# Revit family: Haworth_BeHold_StackOnBookcase
name_source: partatom
category: Furniture Systems
revit_build: Autodesk Revit 2018 (Build: 20170223_1515(x64)
units: mm (PartAtom-declared; Revit-internal decimal feet)

## family parameters
Always vertical = Yes
Cut with Voids When Loaded = No
OmniClass Number = 23.40.70.14.64.21
OmniClass Title = Systems Furniture
Part Type = Normal
Room Calculation Point = No
Round Connector Dimension = Use Diameter
Shared = No
Work Plane-Based = No

## types (6) — shared parameters
Actual Depth = 16 "
Actual Shelf 1 = Yes
Actual Width = 36 "
Assembly Code = E2020200
Base Height = 0.75 "
Cabinet Finish = Haworth _ Laminate _ Beige H-34
Custom Size = No
Description = Haworth - Be_Hold - Upper Storage - Stack on Bookcase
Inset Style Width = 15.81 "
Manufacturer = Haworth
Max. Height = 59 "
Max. Width = 36 "
Min. Height = 20 "
Min. Width = 18 "
Model = Haworth Be_Hold
Mounting Height = 22 "
Panel Thickness = 0.75 "
Revision Number = 1
Shelf Depth = 15.25 "
Shelf Height 3 = 15.25 "
Shelf Width = 34.5 "
Size = Verify Final Dim. w/ Haworth
Standard Depths = 16
Standard Height = 20-59 in.
Standard Widths = 18-36 in. @ 6 in. increments
Sustainability Info = https://www.haworth.com
URL = www.haworth.com
Warranty = http://www.haworth.com
Width = 36 "

## per-type parameters (varying)
| type | Actual Height | Actual Shelf 2 | Actual Shelf 3 | Height | Inset Style | Proud Style | Shelf Height 1 | Shelf Height 2 |
| 28h 36w | 28 " | No | No | 28 " | Yes | No | 10.44 " | 15.25 " |
| 52h 36w | 52 " | Yes | No | 52 " | Yes | No | 18.44 " | 15.25 " |
| 44h 36w | 44 " | Yes | No | 44 " | Yes | No | 10.44 " | 15.25 " |
| 35h 36w | 35 " | No | No | 35 " | Yes | No | 18.44 " | 15.25 " |
| 20h 36w | 20 " | No | No | 20 " | No | Yes | 3.63 " | 15.25 " |
| 59h 36w | 59 " | Yes | Yes | 59 " | Yes | No | 12.75 " | 11.94 " |

## geometry (parser evidence)
native form markers: Sweep x2
no freeform markers — native parametric forms only
